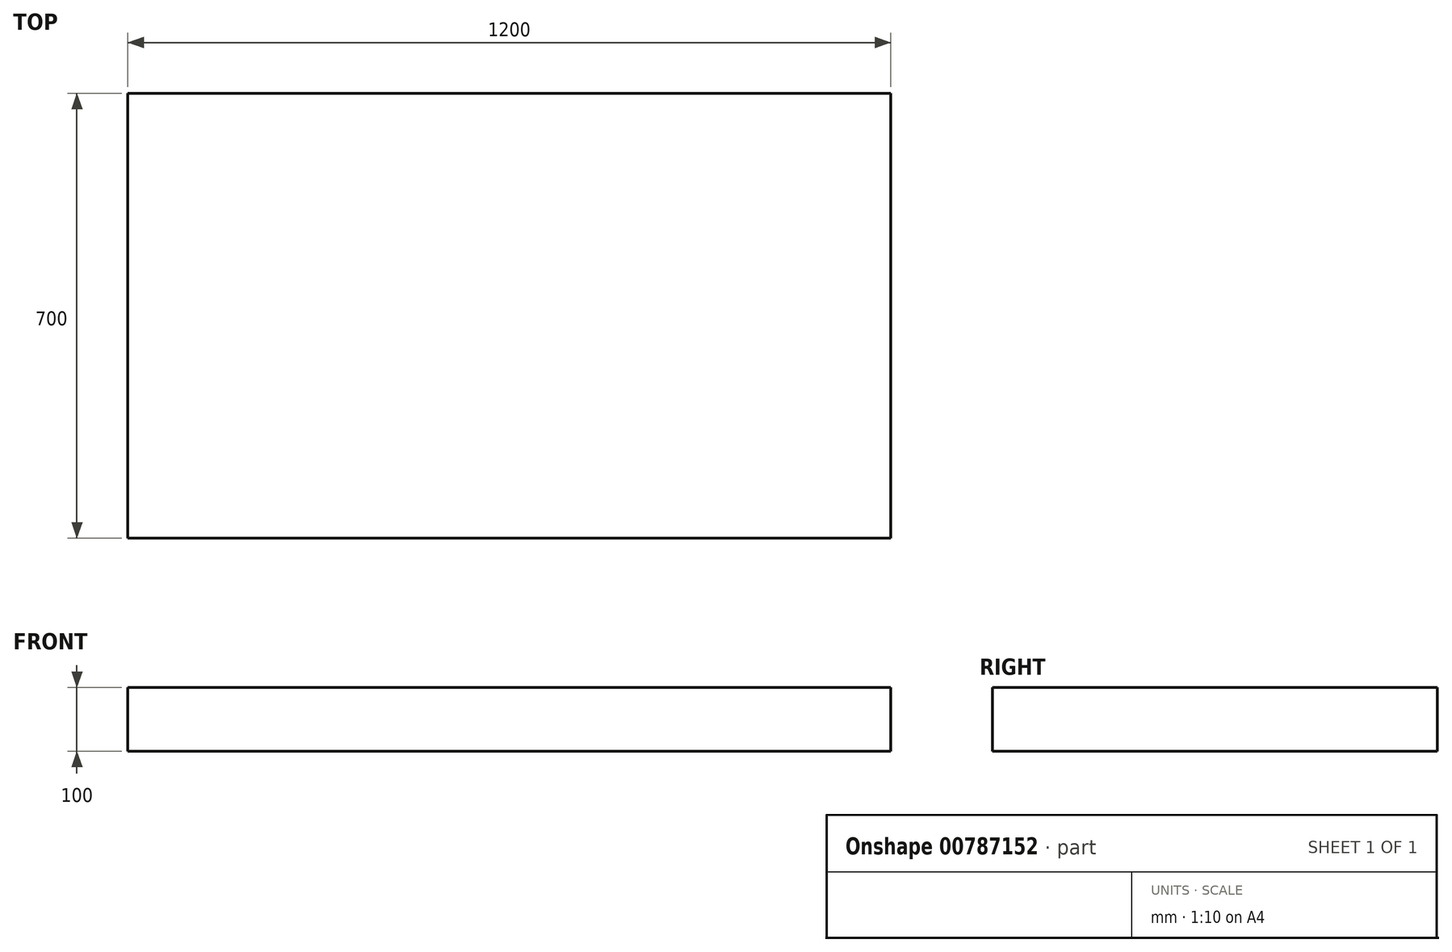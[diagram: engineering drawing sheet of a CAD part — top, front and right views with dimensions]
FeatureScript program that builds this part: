
annotation { "Feature Type Name" : "Feature", "Feature Type Description" : "" }
export const myFeature = defineFeature(function(context is Context, id is Id, definition is map)
    precondition{}
    {
        {
            var Q0;
            Q0=qCreatedBy(makeId("Top.planeOp"),FACE);
            var sketch = newSketch(context, id + "F0", { "sketchPlane" : qUnion([Q0])});
            skLineSegment(sketch, "E0.bottom", {"start": v(0, 0) * mm, "end": v(1200, 0) * mm});
            skLineSegment(sketch, "E0.top", {"start": v(0, 700) * mm, "end": v(1200, 700) * mm});
            skLineSegment(sketch, "E0.left", {"start": v(0, 0) * mm, "end": v(0, 700) * mm});
            skLineSegment(sketch, "E0.right", {"start": v(1200, 0) * mm, "end": v(1200, 700) * mm});
            skSolve(sketch);
        }
        {
            var Q0;
            Q0=makeQuery(id+"F0.imprint","IMPRINT",FACE,{"disambiguationData":[TD([[makeQuery(id+"F0.imprint","IMPRINT",EDGE,{"derivedFrom":sQuery(id+"F0.wireOp",EDGE,"E0.bottom")}),1.0]])]});
            extrude(context, id + "F1", {"entities" : qUnion([Q0]), "depth" : 100 * mm, "offsetDistance" : 25 * mm});
        }
    });
